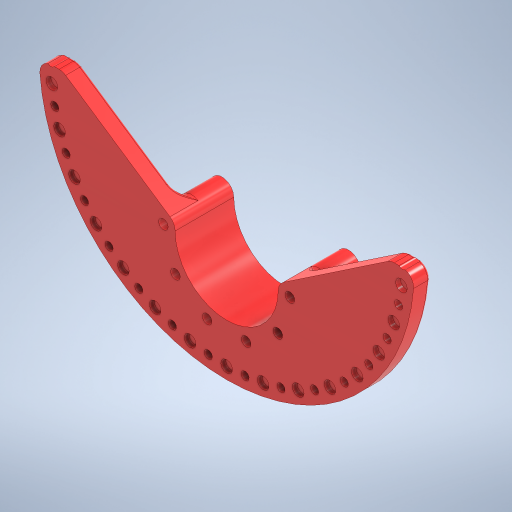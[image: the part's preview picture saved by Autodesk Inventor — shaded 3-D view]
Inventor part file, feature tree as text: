
AUTODESK INVENTOR PART (.ipt)
format: ipt  version: 2024 (Build 280153000, 153)  size: 429,568 bytes
history: native  units: mm
features: sketch x5, fillet x4, hole x3, pattern_circular x3, extrude x2, other x1, projected_geometry x1
ambient origin geometry x8: Origin, YZ Plane, XZ Plane, XY Plane, X Axis, Y Axis, Z Axis, Center Point
bodies: Body1 (feature_tree)
feature tree (19):
  other  "ソリッド1"
  extrude  "押し出し1"  Depth=160.0mm
  hole  "穴1"  [1 undecoded]
  pattern_circular  "円形状パターン1"  [2 undecoded]
  extrude  "押し出し2"  Depth=64.0mm
  hole  "穴2"  [1 undecoded]
  pattern_circular  "円形状パターン2"  [2 undecoded]
  fillet  "フィレット1"  Radius=7.0mm
  fillet  "フィレット2"  Radius=1.047198mm
  fillet  "フィレット3"  Radius=75.0mm
  fillet  "フィレット4"  Radius=300.0mm
  hole  "穴3"  [1 undecoded]
  pattern_circular  "円形状パターン3"  [2 undecoded]
  sketch  "スケッチ1"
  sketch  "スケッチ2"
  sketch  "スケッチ4"
  projected_geometry  "投影ループ2"
  sketch  "スケッチ5"
  sketch  "スケッチ6"
note: 9 required parameter values undecoded (feature->parameter linkage not recoverable at this tier; creation-order binding heuristic only, values carry confidence <= 0.55)
